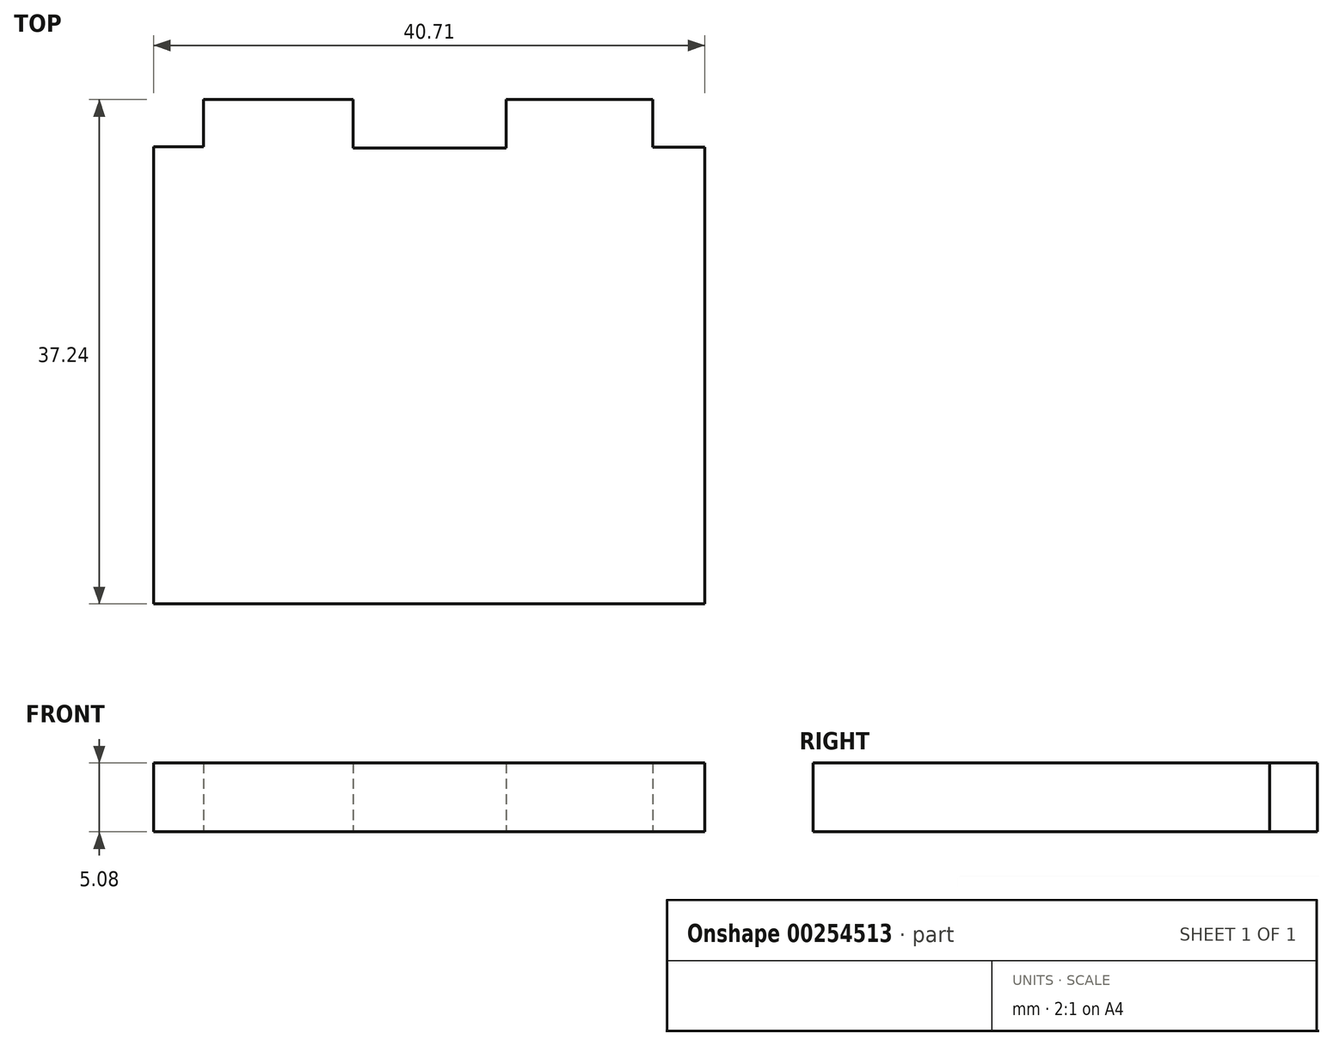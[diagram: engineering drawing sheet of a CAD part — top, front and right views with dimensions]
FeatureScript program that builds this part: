
annotation { "Feature Type Name" : "Feature", "Feature Type Description" : "" }
export const myFeature = defineFeature(function(context is Context, id is Id, definition is map)
    precondition{}
    {
        {
            var Q0;
            Q0=qCreatedBy(makeId("Top.planeOp"),FACE);
            var sketch = newSketch(context, id + "F0", { "sketchPlane" : qUnion([Q0])});
            skLineSegment(sketch, "E0", {"start": v(-33.45, 9.2) * mm, "end": v(-26.8, 16.12) * mm});
            skLineSegment(sketch, "E1", {"start": v(-26.8, 16.12) * mm, "end": v(-22.17, 16.12) * mm});
            skLineSegment(sketch, "E2", {"start": v(-22.17, 16.12) * mm, "end": v(-22.17, 19.99) * mm});
            skLineSegment(sketch, "E3", {"start": v(-22.17, 19.99) * mm, "end": v(-25.8, 19.97) * mm});
            skLineSegment(sketch, "E4", {"start": v(-25.8, 19.97) * mm, "end": v(-25.8, 38.73) * mm});
            skLineSegment(sketch, "E5", {"start": v(-25.8, 38.73) * mm, "end": v(-18.88, 45.9) * mm});
            skLineSegment(sketch, "E6", {"start": v(-18.88, 45.9) * mm, "end": v(14.3, 45.9) * mm});
            skLineSegment(sketch, "E7", {"start": v(14.3, 45.9) * mm, "end": v(22.2, 38.73) * mm});
            skLineSegment(sketch, "E8", {"start": v(22.2, 38.73) * mm, "end": v(22.2, 19.97) * mm});
            skLineSegment(sketch, "E9", {"start": v(22.2, 19.97) * mm, "end": v(18.52, 19.97) * mm});
            skLineSegment(sketch, "E10", {"start": v(18.52, 19.97) * mm, "end": v(18.52, 16.12) * mm});
            skLineSegment(sketch, "E11", {"start": v(18.52, 16.12) * mm, "end": v(22.2, 16.12) * mm});
            skLineSegment(sketch, "E12", {"start": v(22.2, 16.12) * mm, "end": v(29.83, 9.43) * mm});
            skLineSegment(sketch, "E13", {"start": v(29.83, 9.43) * mm, "end": v(29.83, -20.85) * mm});
            skLineSegment(sketch, "E14", {"start": v(29.83, -20.85) * mm, "end": v(22.14, -20.85) * mm});
            skLineSegment(sketch, "E15", {"start": v(22.14, -20.85) * mm, "end": v(22.14, -32.04) * mm});
            skLineSegment(sketch, "E16", {"start": v(22.14, -32.04) * mm, "end": v(19.03, -35.7) * mm});
            skLineSegment(sketch, "E17", {"start": v(19.03, -35.7) * mm, "end": v(3.87, -35.7) * mm});
            skLineSegment(sketch, "E18", {"start": v(3.87, -35.7) * mm, "end": v(3.87, -28.47) * mm});
            skLineSegment(sketch, "E19", {"start": v(3.87, -28.47) * mm, "end": v(-7.29, -28.47) * mm});
            skLineSegment(sketch, "E20", {"start": v(-7.29, -28.47) * mm, "end": v(-7.29, -35.7) * mm});
            skLineSegment(sketch, "E21", {"start": v(-7.29, -35.7) * mm, "end": v(-23.05, -35.7) * mm});
            skLineSegment(sketch, "E22", {"start": v(-23.05, -35.7) * mm, "end": v(-25.8, -32.44) * mm});
            skLineSegment(sketch, "E23", {"start": v(-25.8, -32.44) * mm, "end": v(-25.8, -20.85) * mm});
            skLineSegment(sketch, "E24", {"start": v(-25.8, -20.85) * mm, "end": v(-33.32, -20.85) * mm});
            skLineSegment(sketch, "E25", {"start": v(-33.32, -20.85) * mm, "end": v(-33.45, 9.2) * mm});
            skCircle(sketch, "E26", {"center": v(-11.3, 31.23) * mm, "radius": 5.9 * mm});
            skPoint(sketch, "E26.first.point", {"position": v(-17.19, 30.94) * mm});
            skPoint(sketch, "E26.second.point", {"position": v(-5.4, 31.07) * mm});
            skPoint(sketch, "E26.third.point", {"position": v(-11.26, 25.33) * mm});
            skCircle(sketch, "E27", {"center": v(7.12, 31) * mm, "radius": 5.64 * mm});
            skPoint(sketch, "E27.first.point", {"position": v(1.48, 30.84) * mm});
            skPoint(sketch, "E27.second.point", {"position": v(12.76, 30.78) * mm});
            skPoint(sketch, "E27.third.point", {"position": v(7.1, 36.64) * mm});
            skLineSegment(sketch, "E28.bottom", {"start": v(-14.96, 34.57) * mm, "end": v(-7.5, 34.57) * mm});
            skLineSegment(sketch, "E28.top", {"start": v(-14.96, 27.44) * mm, "end": v(-7.5, 27.44) * mm});
            skLineSegment(sketch, "E28.left", {"start": v(-14.96, 34.57) * mm, "end": v(-14.96, 27.44) * mm});
            skLineSegment(sketch, "E28.right", {"start": v(-7.5, 34.57) * mm, "end": v(-7.5, 27.44) * mm});
            skLineSegment(sketch, "E29.bottom", {"start": v(3.8, 34.28) * mm, "end": v(10.72, 34.28) * mm});
            skLineSegment(sketch, "E29.top", {"start": v(3.8, 27.44) * mm, "end": v(10.72, 27.44) * mm});
            skLineSegment(sketch, "E29.left", {"start": v(3.8, 34.28) * mm, "end": v(3.8, 27.44) * mm});
            skLineSegment(sketch, "E29.right", {"start": v(10.72, 34.28) * mm, "end": v(10.72, 27.44) * mm});
            skLineSegment(sketch, "E30.bottom", {"start": v(7.12, 31) * mm, "end": v(3.8, 31) * mm});
            skLineSegment(sketch, "E30.top", {"start": v(7.12, 34.28) * mm, "end": v(3.8, 34.28) * mm});
            skLineSegment(sketch, "E30.left", {"start": v(7.12, 31) * mm, "end": v(7.12, 34.28) * mm});
            skLineSegment(sketch, "E30.right", {"start": v(3.8, 31) * mm, "end": v(3.8, 34.28) * mm});
            skLineSegment(sketch, "E31.bottom", {"start": v(-11.3, 31.23) * mm, "end": v(-14.96, 31.23) * mm});
            skLineSegment(sketch, "E31.top", {"start": v(-11.3, 34.57) * mm, "end": v(-14.96, 34.57) * mm});
            skLineSegment(sketch, "E31.left", {"start": v(-11.3, 31.23) * mm, "end": v(-11.3, 34.57) * mm});
            skLineSegment(sketch, "E31.right", {"start": v(-14.96, 31.23) * mm, "end": v(-14.96, 34.57) * mm});
            skLineSegment(sketch, "E32.bottom", {"start": v(-3.8, 23.6) * mm, "end": v(0, 23.6) * mm});
            skLineSegment(sketch, "E32.top", {"start": v(-3.8, 19.8) * mm, "end": v(0, 19.8) * mm});
            skLineSegment(sketch, "E32.left", {"start": v(-3.8, 23.6) * mm, "end": v(-3.8, 19.8) * mm});
            skLineSegment(sketch, "E32.right", {"start": v(0, 23.6) * mm, "end": v(0, 19.8) * mm});
            skLineSegment(sketch, "E33.bottom", {"start": v(-7.5, 15.86) * mm, "end": v(3.8, 15.86) * mm});
            skLineSegment(sketch, "E33.top", {"start": v(-7.5, 12.27) * mm, "end": v(3.8, 12.27) * mm});
            skLineSegment(sketch, "E33.left", {"start": v(-7.5, 15.86) * mm, "end": v(-7.5, 12.27) * mm});
            skLineSegment(sketch, "E33.right", {"start": v(3.8, 15.86) * mm, "end": v(3.8, 12.27) * mm});
            skPoint(sketch, "E34.oppositeSnap0", {"position": v(-25.8, -26.64) * mm});
            skLineSegment(sketch, "E34.bottom", {"start": v(-29.45, -9.9) * mm, "end": v(-25.8, -9.9) * mm});
            skLineSegment(sketch, "E34.top", {"start": v(-29.45, -17.27) * mm, "end": v(-25.8, -17.27) * mm});
            skLineSegment(sketch, "E34.left", {"start": v(-29.45, -9.9) * mm, "end": v(-29.45, -17.27) * mm});
            skLineSegment(sketch, "E34.right", {"start": v(-25.8, -9.9) * mm, "end": v(-25.8, -17.27) * mm});
            skLineSegment(sketch, "E35.top", {"start": v(-29.45, 8.74) * mm, "end": v(-25.8, 8.74) * mm});
            skLineSegment(sketch, "E35.left", {"start": v(-29.45, -9.9) * mm, "end": v(-29.45, 8.74) * mm});
            skLineSegment(sketch, "E35.right", {"start": v(-25.8, -9.9) * mm, "end": v(-25.8, 8.74) * mm});
            skLineSegment(sketch, "E36.bottom", {"start": v(22.2, -9.9) * mm, "end": v(25.76, -9.9) * mm});
            skLineSegment(sketch, "E36.top", {"start": v(22.2, -17.27) * mm, "end": v(25.76, -17.27) * mm});
            skLineSegment(sketch, "E36.left", {"start": v(22.2, -9.9) * mm, "end": v(22.2, -17.27) * mm});
            skLineSegment(sketch, "E36.right", {"start": v(25.76, -9.9) * mm, "end": v(25.76, -17.27) * mm});
            skLineSegment(sketch, "E37.top", {"start": v(22.2, 8.7) * mm, "end": v(25.76, 8.7) * mm});
            skLineSegment(sketch, "E37.left", {"start": v(22.2, -9.9) * mm, "end": v(22.2, 8.7) * mm});
            skLineSegment(sketch, "E37.right", {"start": v(25.76, -9.9) * mm, "end": v(25.76, 8.7) * mm});
            skLineSegment(sketch, "E38.bottom", {"start": v(-3.6, -28.47) * mm, "end": v(0, -28.47) * mm});
            skLineSegment(sketch, "E38.top", {"start": v(-3.6, -24.74) * mm, "end": v(0, -24.74) * mm});
            skLineSegment(sketch, "E38.left", {"start": v(-3.6, -28.47) * mm, "end": v(-3.6, -24.74) * mm});
            skLineSegment(sketch, "E38.right", {"start": v(0, -28.47) * mm, "end": v(0, -24.74) * mm});
            skLineSegment(sketch, "E39", {"start": v(-22.24, -24.61) * mm, "end": v(-22.24, -31.85) * mm});
            skLineSegment(sketch, "E40", {"start": v(-22.24, -31.85) * mm, "end": v(-11.06, -31.85) * mm});
            skLineSegment(sketch, "E41", {"start": v(-11.06, -31.85) * mm, "end": v(-11.06, -28.48) * mm});
            skLineSegment(sketch, "E42", {"start": v(-11.06, -28.48) * mm, "end": v(-7.29, -28.47) * mm});
            skLineSegment(sketch, "E43", {"start": v(-7.29, -24.61) * mm, "end": v(-22.24, -24.61) * mm});
            skLineSegment(sketch, "E44", {"start": v(-7.29, -24.61) * mm, "end": v(-7.29, -28.47) * mm});
            skLineSegment(sketch, "E45", {"start": v(3.87, -28.47) * mm, "end": v(3.87, -24.61) * mm});
            skLineSegment(sketch, "E46", {"start": v(3.87, -24.61) * mm, "end": v(18.56, -24.61) * mm});
            skLineSegment(sketch, "E47", {"start": v(18.56, -24.61) * mm, "end": v(18.56, -31.97) * mm});
            skLineSegment(sketch, "E48", {"start": v(18.56, -31.97) * mm, "end": v(7.4, -31.97) * mm});
            skLineSegment(sketch, "E49", {"start": v(7.4, -31.97) * mm, "end": v(7.4, -28.47) * mm});
            skLineSegment(sketch, "E50", {"start": v(7.4, -28.47) * mm, "end": v(3.87, -28.47) * mm});
            skLineSegment(sketch, "E51", {"start": v(-22.17, 19.99) * mm, "end": v(-22.24, 38.23) * mm});
            skLineSegment(sketch, "E52", {"start": v(-22.24, 38.23) * mm, "end": v(-18.48, 38.25) * mm});
            skLineSegment(sketch, "E53", {"start": v(-18.48, 38.25) * mm, "end": v(-18.5, 42.04) * mm});
            skLineSegment(sketch, "E54", {"start": v(-18.5, 42.04) * mm, "end": v(14.76, 42.16) * mm});
            skLineSegment(sketch, "E55", {"start": v(14.76, 42.16) * mm, "end": v(14.78, 38.23) * mm});
            skLineSegment(sketch, "E56", {"start": v(14.78, 38.23) * mm, "end": v(18.52, 38.24) * mm});
            skLineSegment(sketch, "E57", {"start": v(18.52, 38.24) * mm, "end": v(18.52, 19.97) * mm});
            skLineSegment(sketch, "E58", {"start": v(3.8, 15.86) * mm, "end": v(3.8, 19.97) * mm});
            skLineSegment(sketch, "E59", {"start": v(3.8, 19.97) * mm, "end": v(18.52, 19.97) * mm});
            skLineSegment(sketch, "E60", {"start": v(-7.5, 15.86) * mm, "end": v(-7.5, 19.99) * mm});
            skLineSegment(sketch, "E61", {"start": v(-7.5, 19.99) * mm, "end": v(-22.17, 19.99) * mm});
            skLineSegment(sketch, "E62", {"start": v(-22.23, 12.38) * mm, "end": v(-22.23, -21.38) * mm});
            skLineSegment(sketch, "E63", {"start": v(-22.23, -21.38) * mm, "end": v(18.48, -21.38) * mm});
            skLineSegment(sketch, "E64", {"start": v(18.48, -21.38) * mm, "end": v(18.48, 12.34) * mm});
            skLineSegment(sketch, "E65", {"start": v(18.48, 12.34) * mm, "end": v(14.65, 12.34) * mm});
            skLineSegment(sketch, "E66", {"start": v(14.65, 12.34) * mm, "end": v(14.65, 15.86) * mm});
            skLineSegment(sketch, "E67", {"start": v(14.65, 15.86) * mm, "end": v(3.8, 15.86) * mm});
            skLineSegment(sketch, "E68", {"start": v(-22.23, 12.38) * mm, "end": v(-18.53, 12.38) * mm});
            skLineSegment(sketch, "E69", {"start": v(-18.53, 12.38) * mm, "end": v(-18.53, 15.86) * mm});
            skLineSegment(sketch, "E70", {"start": v(-18.53, 15.86) * mm, "end": v(-7.5, 15.86) * mm});
            skLineSegment(sketch, "E71.bottom", {"start": v(-7.42, -28.31) * mm, "end": v(-7.13, -28.31) * mm});
            skLineSegment(sketch, "E71.top", {"start": v(-7.42, -28.63) * mm, "end": v(-7.13, -28.63) * mm});
            skLineSegment(sketch, "E71.left", {"start": v(-7.42, -28.31) * mm, "end": v(-7.42, -28.63) * mm});
            skLineSegment(sketch, "E71.right", {"start": v(-7.13, -28.31) * mm, "end": v(-7.13, -28.63) * mm});
            skLineSegment(sketch, "E72.bottom", {"start": v(3.95, -28.38) * mm, "end": v(3.78, -28.38) * mm});
            skLineSegment(sketch, "E72.top", {"start": v(3.95, -28.56) * mm, "end": v(3.78, -28.56) * mm});
            skLineSegment(sketch, "E72.left", {"start": v(3.95, -28.38) * mm, "end": v(3.95, -28.56) * mm});
            skLineSegment(sketch, "E72.right", {"start": v(3.78, -28.38) * mm, "end": v(3.78, -28.56) * mm});
            skSolve(sketch);
        }
        {
            var Q0;
            Q0=makeQuery(id+"F0.imprint","IMPRINT",FACE,{"disambiguationData":[TD([[makeQuery(id+"F0.imprint","IMPRINT",EDGE,{"derivedFrom":sQuery(id+"F0.wireOp",EDGE,"E33.top")}),-1.0]])]});
            extrude(context, id + "F1", {"entities" : qUnion([Q0]), "depth" : 5.08 * mm});
        }
    });
